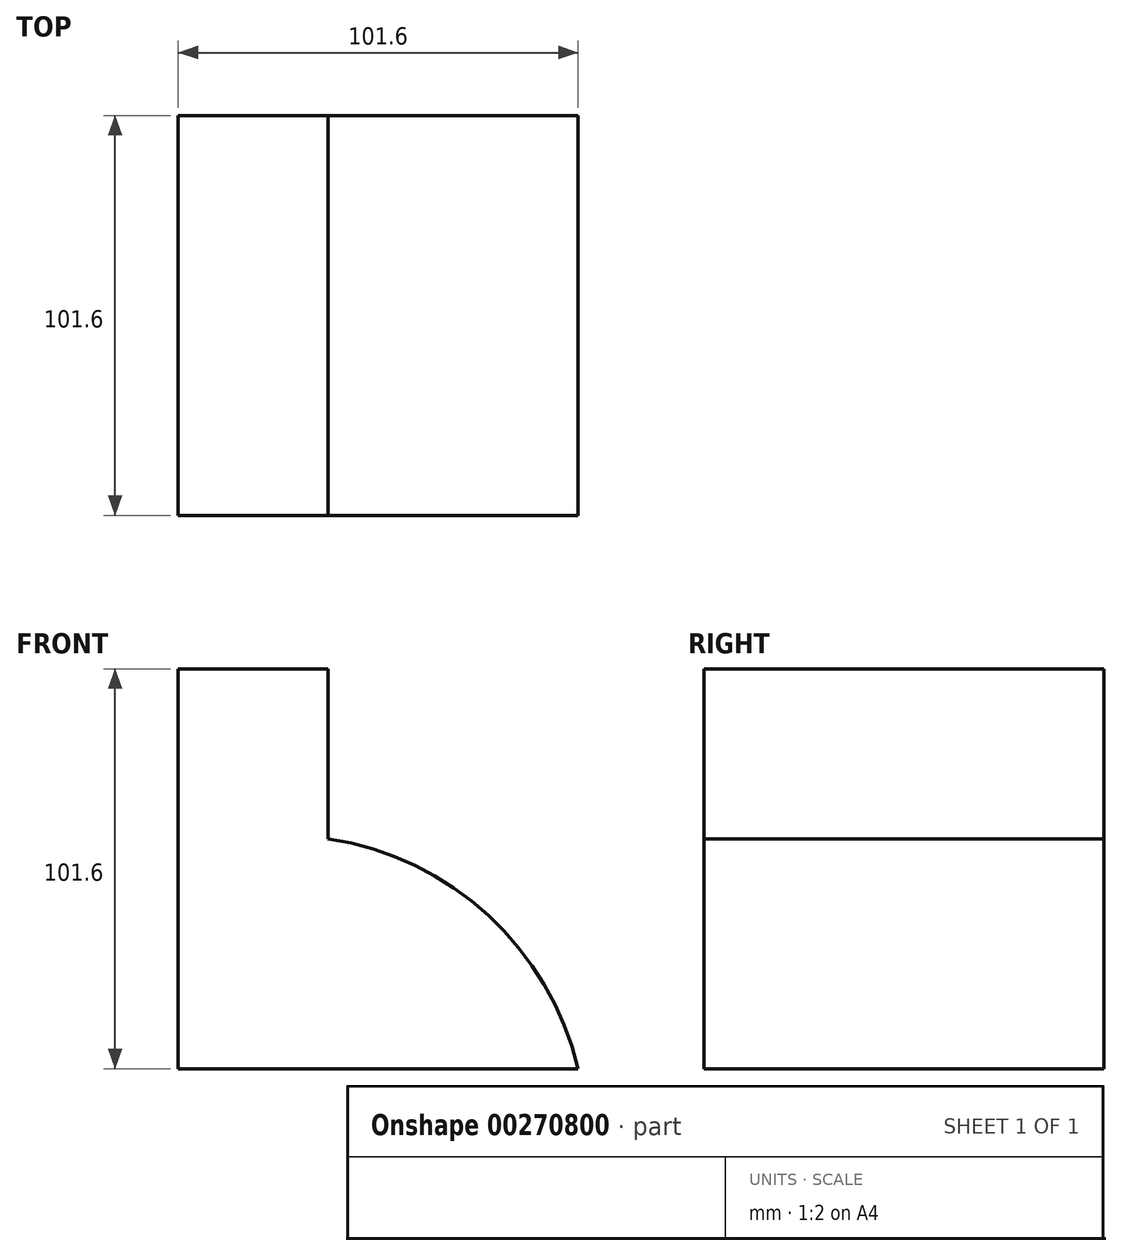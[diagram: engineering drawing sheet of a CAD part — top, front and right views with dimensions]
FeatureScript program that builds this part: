
annotation { "Feature Type Name" : "Feature", "Feature Type Description" : "" }
export const myFeature = defineFeature(function(context is Context, id is Id, definition is map)
    precondition{}
    {
        {
            var Q0;
            Q0=qCreatedBy(makeId("Front.planeOp"),FACE);
            var sketch = newSketch(context, id + "F0", { "sketchPlane" : qUnion([Q0])});
            skLineSegment(sketch, "E0", {"start": v(-35.8, 43.18) * mm, "end": v(-35.8, -58.42) * mm});
            skLineSegment(sketch, "E1", {"start": v(-35.8, -58.42) * mm, "end": v(65.8, -58.42) * mm});
            skLineSegment(sketch, "E2", {"start": v(-35.8, 43.18) * mm, "end": v(2.3, 43.18) * mm});
            skLineSegment(sketch, "E3", {"start": v(2.3, 43.18) * mm, "end": v(2.3, 0) * mm});
            skArc(sketch, "E4", {"start": v(65.8, -58.42) * mm, "mid": v(42.98, -19.5) * mm, "end": v(2.3, 0) * mm});
            skSolve(sketch);
        }
        {
            var Q0;
            Q0 = qSketchRegion(id + "F0", true);
            extrude(context, id + "F1", {"entities" : qUnion([Q0]), "depth" : 101.6 * mm});
        }
    });
